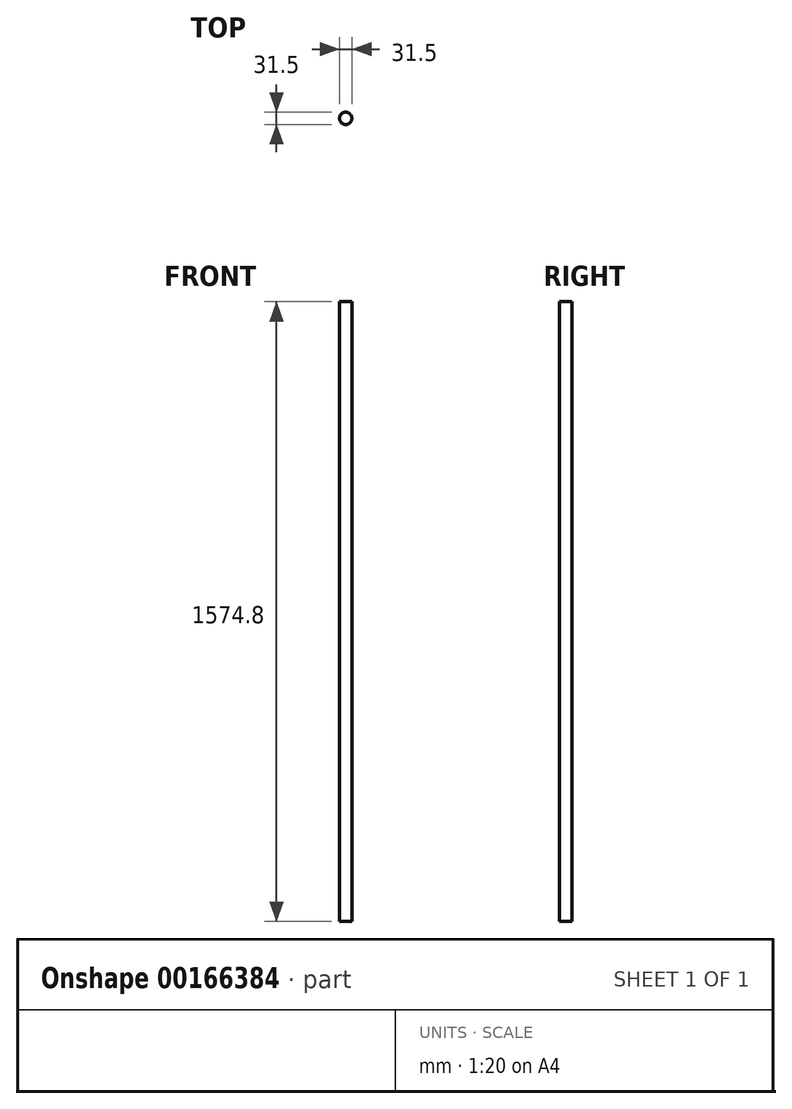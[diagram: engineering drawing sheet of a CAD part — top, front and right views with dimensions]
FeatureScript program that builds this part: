
annotation { "Feature Type Name" : "Feature", "Feature Type Description" : "" }
export const myFeature = defineFeature(function(context is Context, id is Id, definition is map)
    precondition{}
    {
        {
            var Q0;
            Q0=qCreatedBy(makeId("Top.planeOp"),FACE);
            var sketch = newSketch(context, id + "F0", { "sketchPlane" : qUnion([Q0])});
            skCircle(sketch, "E0", {"center": v(0, 0) * mm, "radius": 15.75 * mm});
            skSolve(sketch);
        }
        {
            var Q0;
            Q0=makeQuery(id+"F0.imprint","IMPRINT",FACE,{"disambiguationData":[TD([[makeQuery(id+"F0.imprint","IMPRINT",EDGE,{"derivedFrom":sQuery(id+"F0.wireOp",EDGE,"E0")}),1.0]])]});
            extrude(context, id + "F1", {"entities" : qUnion([Q0]), "depth" : 1574.8 * mm});
        }
    });
